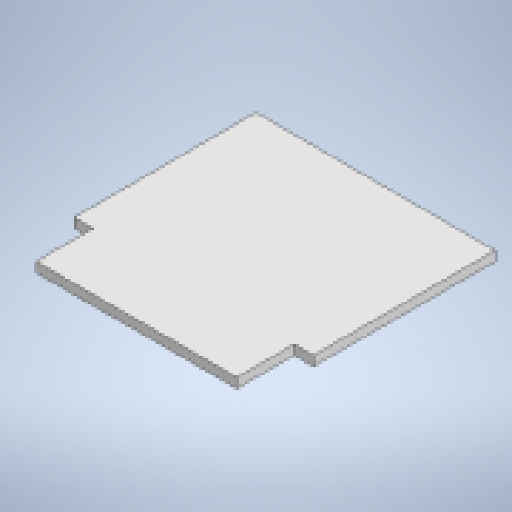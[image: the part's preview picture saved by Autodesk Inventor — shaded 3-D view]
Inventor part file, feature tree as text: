
AUTODESK INVENTOR PART (.ipt)
format: ipt  version: 2023 (Build 270158000, 158)  size: 227,328 bytes
history: native  units: mm
features: other x3, extrude x3, sketch x3, projected_geometry x2, reference x1
ambient origin geometry x8: Origin, YZ Plane, XZ Plane, XY Plane, X Axis, Y Axis, Z Axis, Center Point
bodies: Body1 (feature_tree)
feature tree (12):
  other  "Bryła1"
  extrude  "Wyciągnięcie proste1"  Depth=50.0mm
  extrude  "Wyciągnięcie proste2"  Depth=50.0mm
  extrude  "Wyciągnięcie proste3"  Depth=2.0mm TaperAngle=0.0deg
  sketch  "Szkic1"
  sketch  "Szkic2"
  projected_geometry  "Pętla rzutowana1"
  sketch  "Szkic3"
  reference  "Odniesienie1"
  projected_geometry  "Pętla rzutowana2"
  other  "Zespół2"
  other  "nozzz:1"
